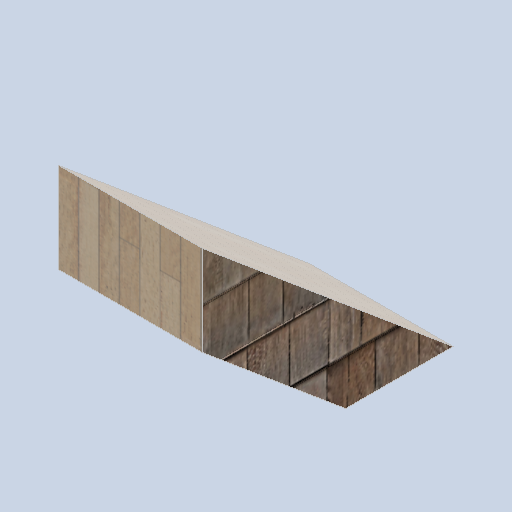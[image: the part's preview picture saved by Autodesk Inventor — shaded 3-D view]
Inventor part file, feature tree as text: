
AUTODESK INVENTOR PART (.ipt)
format: ipt  version: 2024.2 (Build 282272000, 272)  size: 329,216 bytes
history: native  units: mm
features: extrude x1, sketch x1
ambient origin geometry x8: Origin, YZ Plane, XZ Plane, XY Plane, X Axis, Y Axis, Z Axis, Center Point
bodies: Body1 (feature_tree)
feature tree (2):
  extrude  "Extrusion3"  Depth=400.0mm
  sketch  "Sketch1"  dims[d2=300.0mm d11=8.726646mm d12=8.726646mm d13=400.0mm d14=0.0mm]
